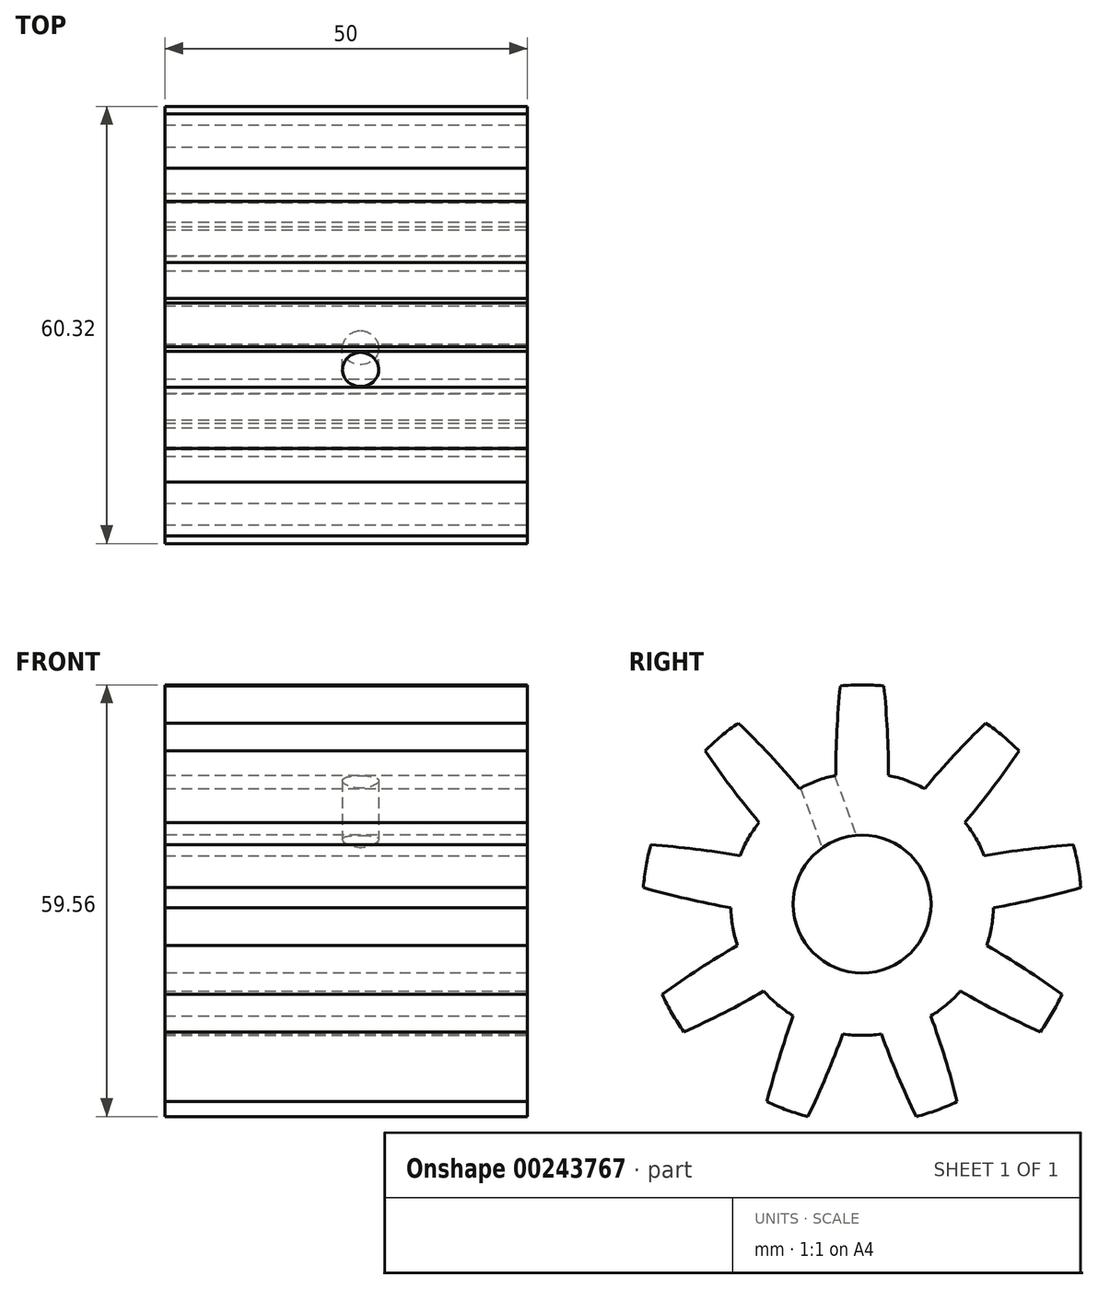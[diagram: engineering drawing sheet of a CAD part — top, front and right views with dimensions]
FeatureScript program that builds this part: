
annotation { "Feature Type Name" : "Feature", "Feature Type Description" : "" }
export const myFeature = defineFeature(function(context is Context, id is Id, definition is map)
    precondition{}
    {
        {
            var Q0;
            Q0=qCreatedBy(makeId("Front.planeOp"),FACE);
            var sketch = newSketch(context, id + "F0", { "sketchPlane" : qUnion([Q0])});
            skLineSegment(sketch, "E0.bottom", {"start": v(-50, 30.25) * mm, "end": v(0, 30.25) * mm});
            skLineSegment(sketch, "E0.top", {"start": v(-50, 9.5) * mm, "end": v(0, 9.5) * mm});
            skLineSegment(sketch, "E0.left", {"start": v(-50, 30.25) * mm, "end": v(-50, 9.5) * mm});
            skLineSegment(sketch, "E0.right", {"start": v(0, 30.25) * mm, "end": v(0, 9.5) * mm});
            skLineSegment(sketch, "E1", {"start": v(-55.21, 0) * mm, "end": v(15.07, 0) * mm, "construction": true});
            skSolve(sketch);
        }
        {
            var Q0;
            Q0=makeQuery(id+"F0.imprint","IMPRINT",FACE,{"disambiguationData":[TD([[makeQuery(id+"F0.imprint","IMPRINT",EDGE,{"derivedFrom":sQuery(id+"F0.wireOp",EDGE,"E0.bottom")}),-1.0]])]});
            var Q1;
            Q1=sQuery(id+"F0.wireOp",EDGE,"E1");
            revolve(context, id + "F1", {"entities" : qUnion([Q0]), "axis" : qUnion([Q1]), "revolveType" : RevolveType.FULL});
        }
        {
            var Q0;
            Q0=makeQuery(id+"F1.opRevolve","SWEPT_FACE",FACE,{"disambiguationData":[OSD([sQuery(id+"F0.wireOp",EDGE,"E0.right")])]});
            var sketch = newSketch(context, id + "F2", { "sketchPlane" : qUnion([Q0])});
            skLineSegment(sketch, "E2", {"start": v(0, 0) * mm, "end": v(0, 38.44) * mm, "construction": true});
            skArc(sketch, "E3", {"start": v(-3.64, 17.75) * mm, "mid": v(-6.2, 17.03) * mm, "end": v(-8.62, 15.94) * mm});
            skLineSegment(sketch, "E4", {"start": v(0, 0) * mm, "end": v(-6.42, 36.44) * mm, "construction": true});
            skLineSegment(sketch, "E5", {"start": v(0, 0) * mm, "end": v(-11.96, 32.87) * mm, "construction": true});
            skArc(sketch, "E6", {"start": v(-3, 30.1) * mm, "mid": v(-3.48, 23.93) * mm, "end": v(-3.64, 17.75) * mm});
            skArc(sketch, "E7.MirrorCS", {"start": v(-17.05, 24.99) * mm, "mid": v(-12.72, 20.57) * mm, "end": v(-8.62, 15.94) * mm});
            skArc(sketch, "E8", {"start": v(-3, 30.1) * mm, "mid": v(-10.35, 28.43) * mm, "end": v(-17.05, 24.99) * mm});
            skSolve(sketch);
        }
        {
            var Q0;
            Q0 = qSketchRegion(id + "F2", true);
            extrude(context, id + "F3", {"entities" : qUnion([Q0]), "operationType" : NewBodyOperationType.REMOVE, "endBound" : BoundingType.THROUGH_ALL, "oppositeDirection" : true, "depth" : 25 * mm});
        }
        {
            var Q0;
            Q0=makeQuery(id+"F3.boolean.opBoolean","COPY",FACE,{"derivedFrom":makeQuery(id+"F3.opExtrude","SWEPT_FACE",FACE,{"disambiguationData":[OSD([sQuery(id+"F2.wireOp",EDGE,"E6")])]})});
            var Q1;
            Q1=makeQuery(id+"F3.boolean.opBoolean","COPY",FACE,{"derivedFrom":makeQuery(id+"F3.opExtrude","SWEPT_FACE",FACE,{"disambiguationData":[OSD([sQuery(id+"F2.wireOp",EDGE,"E3")])]})});
            var Q2;
            Q2=makeQuery(id+"F3.boolean.opBoolean","COPY",FACE,{"derivedFrom":makeQuery(id+"F3.opExtrude","SWEPT_FACE",FACE,{"disambiguationData":[OSD([sQuery(id+"F2.wireOp",EDGE,"E7.MirrorCS")])]})});
            var Q3;
            Q3=sQuery(id+"F0.wireOp",EDGE,"E1");
            circularPattern(context, id + "F4", {"patternType" : PatternType.FACE, "faces" : qUnion([Q0, Q1, Q2]), "axis" : qUnion([Q3]), "angle" : 360 * degree, "instanceCount" : 9, "equalSpace" : true});
        }
        {
            var Q0;
            Q0=qCreatedBy(makeId("Right.planeOp"),FACE);
            cPlane(context, id + "F5", {"entities" : qUnion([Q0]), "cplaneType" : CPlaneType.OFFSET, "offset" : 23 * mm, "oppositeDirection" : true, "width" : 150 * mm, "height" : 150 * mm});
        }
        {
            var Q0;
            Q0=qCreatedBy(id+"F5.planeOp",FACE);
            var sketch = newSketch(context, id + "F6", { "sketchPlane" : qUnion([Q0])});
            skArc(sketch, "E9.0", {"start": v(-3.64, 17.75) * mm, "mid": v(-6.2, 17.03) * mm, "end": v(-8.62, 15.94) * mm, "construction": true});
            skPoint(sketch, "E10", {"position": v(-6.2, 17.03) * mm});
            skLineSegment(sketch, "E11", {"start": v(-24.67, 10.3) * mm, "end": v(9.56, 22.76) * mm, "construction": true});
            skLineSegment(sketch, "E12", {"start": v(-7.59, 20.85) * mm, "end": v(0, 0) * mm, "construction": true});
            skLineSegment(sketch, "E13", {"start": v(-6.88, 18.9) * mm, "end": v(-4.53, 19.76) * mm});
            skLineSegment(sketch, "E14", {"start": v(-4.53, 19.76) * mm, "end": v(-0.43, 8.49) * mm});
            skLineSegment(sketch, "E15", {"start": v(-0.43, 8.49) * mm, "end": v(-2.78, 7.63) * mm});
            skLineSegment(sketch, "E16", {"start": v(-2.78, 7.63) * mm, "end": v(-6.88, 18.9) * mm});
            skSolve(sketch);
        }
        {
            var Q0;
            Q0=makeQuery(id+"F6.imprint","IMPRINT",FACE,{"disambiguationData":[TD([[makeQuery(id+"F6.imprint","IMPRINT",EDGE,{"derivedFrom":sQuery(id+"F6.wireOp",EDGE,"E13")}),-1.0]])]});
            var Q1;
            Q1=sQuery(id+"F6.wireOp",EDGE,"E12");
            revolve(context, id + "F7", {"operationType" : NewBodyOperationType.REMOVE, "entities" : qUnion([Q0]), "axis" : qUnion([Q1]), "revolveType" : RevolveType.FULL, "oppositeDirection" : true});
        }
    });
